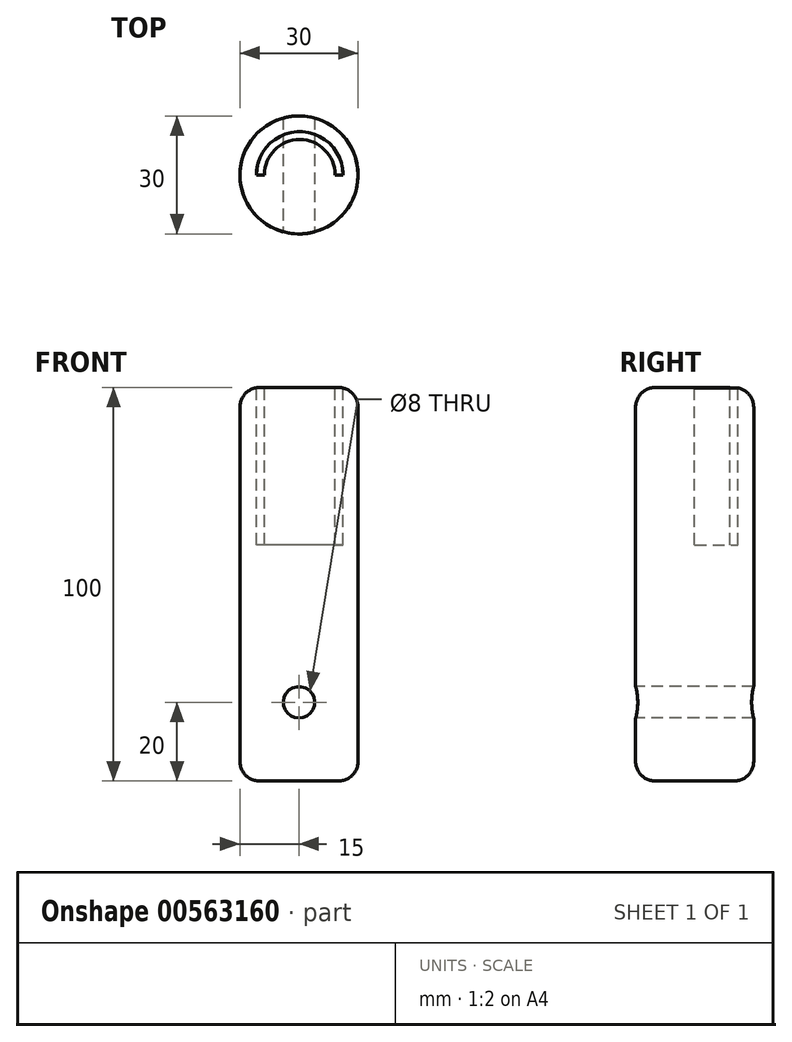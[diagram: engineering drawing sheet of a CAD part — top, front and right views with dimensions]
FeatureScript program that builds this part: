
annotation { "Feature Type Name" : "Feature", "Feature Type Description" : "" }
export const myFeature = defineFeature(function(context is Context, id is Id, definition is map)
    precondition{}
    {
        {
            var Q0;
            Q0=qCreatedBy(makeId("Top.planeOp"),FACE);
            var sketch = newSketch(context, id + "F0", { "sketchPlane" : qUnion([Q0])});
            skCircle(sketch, "E0", {"center": v(0, 0) * mm, "radius": 15 * mm});
            skSolve(sketch);
        }
        {
            var Q0;
            Q0 = qSketchRegion(id + "F0", true);
            extrude(context, id + "F1", {"entities" : qUnion([Q0]), "depth" : 100 * mm, "offsetDistance" : 25 * mm});
        }
        {
            var Q0;
            Q0=makeQuery(id+"F1.opExtrude","CAP_FACE",FACE,{"disambiguationData":[OSD([sQuery(id+"F0.wireOp",EDGE,"E0")])],"isStart":false});
            var sketch = newSketch(context, id + "F2", { "sketchPlane" : qUnion([Q0])});
            skArc(sketch, "E1", {"start": v(11.18, 0) * mm, "mid": v(0.18, 11) * mm, "end": v(-10.82, 0) * mm});
            skArc(sketch, "E2", {"start": v(9.18, 0) * mm, "mid": v(0.18, 9) * mm, "end": v(-8.82, 0) * mm});
            skLineSegment(sketch, "E3", {"start": v(-8.82, 0) * mm, "end": v(-10.82, 0) * mm});
            skLineSegment(sketch, "E4", {"start": v(9.18, 0) * mm, "end": v(11.18, 0) * mm});
            skSolve(sketch);
        }
        {
            var Q0;
            Q0 = qSketchRegion(id + "F2", true);
            extrude(context, id + "F3", {"entities" : qUnion([Q0]), "operationType" : NewBodyOperationType.REMOVE, "oppositeDirection" : true, "depth" : 40 * mm, "offsetDistance" : 25 * mm});
        }
        {
            var Q0;
            Q0=makeQuery(id+"F1.opExtrude","CAP_EDGE",EDGE,{"disambiguationData":[OSD([sQuery(id+"F0.wireOp",EDGE,"E0")])],"isStart":false});
            var Q1;
            Q1=makeQuery(id+"F1.opExtrude","CAP_EDGE",EDGE,{"disambiguationData":[OSD([sQuery(id+"F0.wireOp",EDGE,"E0")])],"isStart":true});
            fillet(context, id + "F4", {"entities" : qUnion([Q0, Q1]), "radius" : 5 * mm, "tangentPropagation" : true, "allowEdgeOverflow" : false});
        }
        {
            var Q0;
            Q0=qCreatedBy(makeId("Front.planeOp"),FACE);
            var sketch = newSketch(context, id + "F5", { "sketchPlane" : qUnion([Q0])});
            skCircle(sketch, "E5", {"center": v(0, 20) * mm, "radius": 4 * mm});
            skSolve(sketch);
        }
        {
            var Q0;
            Q0 = qSketchRegion(id + "F5", true);
            extrude(context, id + "F6", {"entities" : qUnion([Q0]), "operationType" : NewBodyOperationType.REMOVE, "oppositeDirection" : true, "depth" : 25 * mm, "offsetDistance" : 25 * mm, "hasSecondDirection" : true, "secondDirectionOppositeDirection" : false, "secondDirectionDepth" : 25 * mm});
        }
    });
